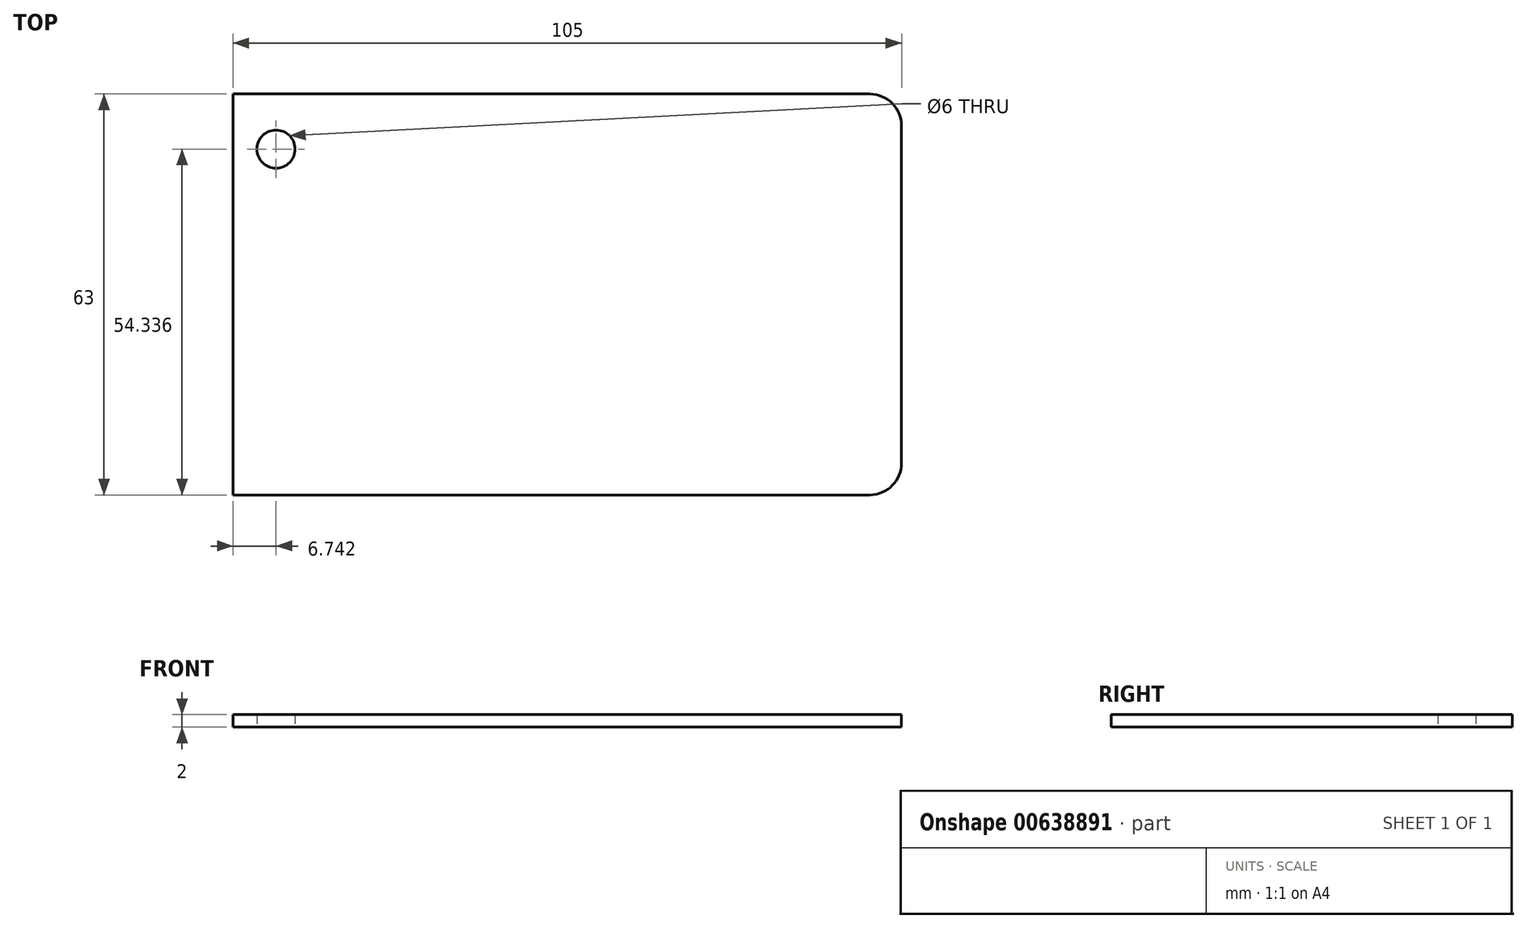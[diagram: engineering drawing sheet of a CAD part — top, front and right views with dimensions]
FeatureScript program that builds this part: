
annotation { "Feature Type Name" : "Feature", "Feature Type Description" : "" }
export const myFeature = defineFeature(function(context is Context, id is Id, definition is map)
    precondition{}
    {
        {
            var Q0;
            Q0=qCreatedBy(makeId("Top.planeOp"),FACE);
            var sketch = newSketch(context, id + "F0", { "sketchPlane" : qUnion([Q0])});
            skArc(sketch, "E0.0", {"start": v(56.28, 24.57) * mm, "mid": v(54.81, 28.1) * mm, "end": v(51.28, 29.57) * mm});
            skLineSegment(sketch, "E0.1", {"start": v(56.28, -28.43) * mm, "end": v(56.28, 24.57) * mm});
            skLineSegment(sketch, "E0.2", {"start": v(51.28, 29.57) * mm, "end": v(-48.72, 29.57) * mm});
            skArc(sketch, "E0.3", {"start": v(51.28, -33.43) * mm, "mid": v(54.81, -31.96) * mm, "end": v(56.28, -28.43) * mm});
            skLineSegment(sketch, "E0.7", {"start": v(51.28, -33.43) * mm, "end": v(-48.72, -33.43) * mm});
            skCircle(sketch, "E1", {"center": v(-41.98, 20.9) * mm, "radius": 3 * mm});
            skLineSegment(sketch, "E2", {"start": v(-48.72, 29.57) * mm, "end": v(-48.72, -33.43) * mm});
            skSolve(sketch);
        }
        {
            var Q0;
            Q0=makeQuery(id+"F0.imprint","IMPRINT",FACE,{"disambiguationData":[TD([[makeQuery(id+"F0.imprint","IMPRINT",EDGE,{"derivedFrom":sQuery(id+"F0.wireOp",EDGE,"E0.0")}),1.0]])]});
            extrude(context, id + "F1", {"entities" : qUnion([Q0]), "depth" : 2 * mm, "offsetDistance" : 25 * mm});
        }
    });
